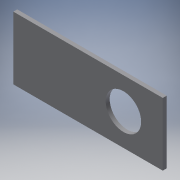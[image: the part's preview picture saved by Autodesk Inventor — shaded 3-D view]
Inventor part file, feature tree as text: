
AUTODESK INVENTOR PART (.ipt)
format: ipt  version: 2016 (Build 200138000, 138)  size: 105,984 bytes
history: native  units: in
note: dims shown in document units (in); Inventor stores cm internally (conversion verified against a paired STEP export)
features: extrude x2, sketch x2
ambient origin geometry x8: Origin, YZ Plane, XZ Plane, XY Plane, X Axis, Y Axis, Z Axis, Center Point
bodies: Solid1 (feature_tree)
feature tree (4):
  extrude  "Extrusion1"  Depth=2.0in
  extrude  "Extrusion2"  Depth=0.125in
  sketch  "Sketch1"  dims[d0=4.75in d1=2.0in]
  sketch  "Sketch2"  dims[d2=1.125in d3=1.25in d4=1.0in d5=0.125in d6=0.0in d7=0.2656in d8=0.2656in d9=0.5in d10=1.5in d11=0.5in d12=0.5in d13=0.125in d14=0.0in]
